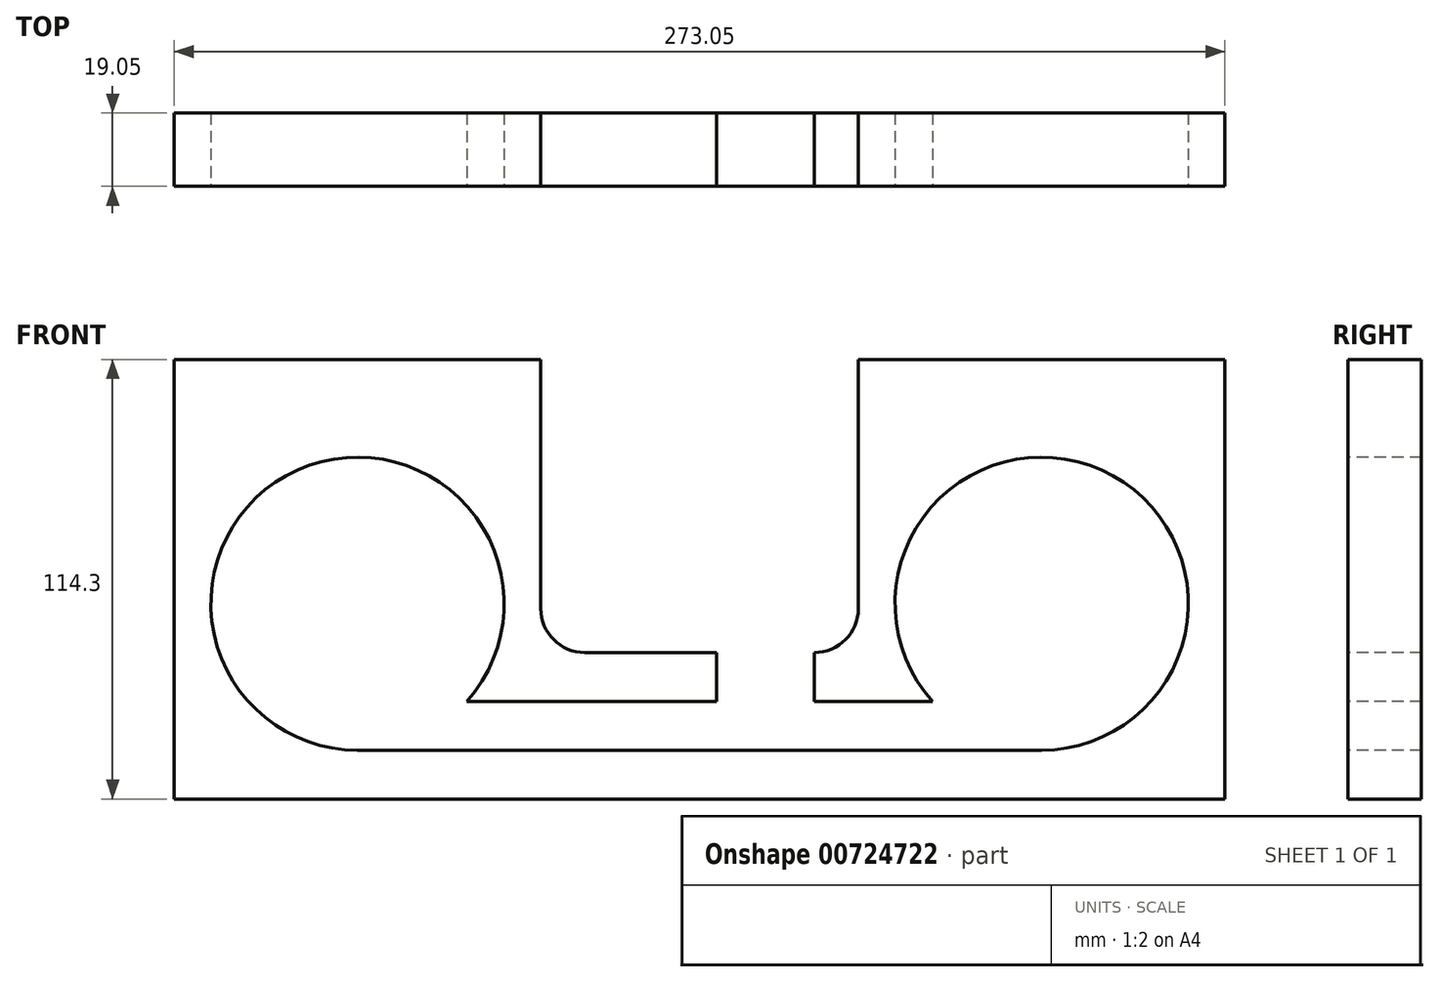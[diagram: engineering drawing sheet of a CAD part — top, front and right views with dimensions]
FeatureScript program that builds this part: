
annotation { "Feature Type Name" : "Feature", "Feature Type Description" : "" }
export const myFeature = defineFeature(function(context is Context, id is Id, definition is map)
    precondition{}
    {
        {
            var Q0;
            Q0=qCreatedBy(makeId("Front.planeOp"),FACE);
            var sketch = newSketch(context, id + "F0", { "sketchPlane" : qUnion([Q0])});
            skLineSegment(sketch, "E0.bottom", {"start": v(0, 0) * mm, "end": v(273.05, 0) * mm});
            skLineSegment(sketch, "E0.top", {"start": v(0, 114.3) * mm, "end": v(273.05, 114.3) * mm});
            skLineSegment(sketch, "E0.left", {"start": v(0, 0) * mm, "end": v(0, 114.3) * mm});
            skLineSegment(sketch, "E0.right", {"start": v(273.05, 0) * mm, "end": v(273.05, 114.3) * mm});
            skSolve(sketch);
        }
        {
            var Q0;
            Q0=qSketchRegion(id+"F0",true);
            extrude(context, id + "F1", {"entities" : qUnion([Q0]), "depth" : 19.05 * mm, "offsetDistance" : 25.4 * mm});
        }
        {
            var Q0;
            Q0=makeQuery(id+"F1.opExtrude","CAP_FACE",FACE,{"disambiguationData":[OSD([sQuery(id+"F0.wireOp",EDGE,"E0.bottom"),sQuery(id+"F0.wireOp",EDGE,"E0.top"),sQuery(id+"F0.wireOp",EDGE,"E0.left"),sQuery(id+"F0.wireOp",EDGE,"E0.right")])],"isStart":false});
            var sketch = newSketch(context, id + "F2", { "sketchPlane" : qUnion([Q0])});
            skCircle(sketch, "E1", {"center": v(47.63, 50.8) * mm, "radius": 38.1 * mm});
            skCircle(sketch, "E2", {"center": v(225.43, 50.8) * mm, "radius": 38.1 * mm});
            skSolve(sketch);
        }
        {
            var Q0;
            Q0=qSketchRegion(id+"F2",true);
            extrude(context, id + "F3", {"entities" : qUnion([Q0]), "operationType" : NewBodyOperationType.REMOVE, "oppositeDirection" : true, "depth" : 25.4 * mm, "offsetDistance" : 25.4 * mm});
        }
        {
            var Q0;
            Q0=makeQuery(id+"F1.opExtrude","CAP_FACE",FACE,{"disambiguationData":[OSD([sQuery(id+"F0.wireOp",EDGE,"E0.bottom"),sQuery(id+"F0.wireOp",EDGE,"E0.top"),sQuery(id+"F0.wireOp",EDGE,"E0.left"),sQuery(id+"F0.wireOp",EDGE,"E0.right")])],"isStart":false});
            var sketch = newSketch(context, id + "F4", { "sketchPlane" : qUnion([Q0])});
            skLineSegment(sketch, "E3", {"start": v(95.25, 114.3) * mm, "end": v(95.25, 49.53) * mm});
            skLineSegment(sketch, "E4", {"start": v(106.68, 38.1) * mm, "end": v(166.37, 38.1) * mm});
            skLineSegment(sketch, "E5", {"start": v(177.8, 49.53) * mm, "end": v(177.8, 114.3) * mm});
            skPoint(sketch, "E6.visualSharp", {"position": v(95.25, 38.1) * mm});
            skArc(sketch, "E6.filletArc", {"start": v(95.25, 49.53) * mm, "mid": v(98.6, 41.45) * mm, "end": v(106.68, 38.1) * mm});
            skPoint(sketch, "E7.visualSharp", {"position": v(177.8, 38.1) * mm});
            skArc(sketch, "E7.filletArc", {"start": v(166.37, 38.1) * mm, "mid": v(174.45, 41.45) * mm, "end": v(177.8, 49.53) * mm});
            skSolve(sketch);
        }
        {
            var Q0;
            Q0=qSketchRegion(id+"F4",true);
            var Q1;
            {var subQ1=sQuery(id+"F4.wireOp",EDGE,"E3");Q1=makeQuery(id+"F4.imprint","IMPRINT",FACE,{"disambiguationData":[TD([[makeQuery(id+"F4.imprint","IMPRINT",EDGE,{"derivedFrom":subQ1}),1.0]])]});}
            extrude(context, id + "F5", {"entities" : qUnion([Q0, Q1]), "operationType" : NewBodyOperationType.REMOVE, "oppositeDirection" : true, "depth" : 25.4 * mm, "offsetDistance" : 25.4 * mm});
        }
        {
            var Q0;
            Q0=makeQuery(id+"F1.opExtrude","CAP_FACE",FACE,{"disambiguationData":[OSD([sQuery(id+"F0.wireOp",EDGE,"E0.bottom"),sQuery(id+"F0.wireOp",EDGE,"E0.top"),sQuery(id+"F0.wireOp",EDGE,"E0.left"),sQuery(id+"F0.wireOp",EDGE,"E0.right")])],"isStart":false});
            var sketch = newSketch(context, id + "F6", { "sketchPlane" : qUnion([Q0])});
            skLineSegment(sketch, "E8", {"start": v(140.97, 38.1) * mm, "end": v(140.97, 25.4) * mm});
            skLineSegment(sketch, "E9", {"start": v(140.97, 25.4) * mm, "end": v(76.02, 25.4) * mm});
            skLineSegment(sketch, "E10", {"start": v(225.43, 12.7) * mm, "end": v(197.03, 25.4) * mm});
            skLineSegment(sketch, "E11", {"start": v(197.03, 25.4) * mm, "end": v(166.37, 25.4) * mm});
            skLineSegment(sketch, "E12", {"start": v(166.37, 25.4) * mm, "end": v(166.37, 38.1) * mm});
            skLineSegment(sketch, "E13", {"start": v(76.02, 25.4) * mm, "end": v(47.63, 12.7) * mm});
            skLineSegment(sketch, "E14", {"start": v(47.63, 12.7) * mm, "end": v(225.43, 12.7) * mm});
            skSolve(sketch);
        }
        {
            var Q0;
            Q0=qSketchRegion(id+"F6",true);
            var Q1;
            {var subQ3=sQuery(id+"F6.wireOp",EDGE,"E8");Q1=makeQuery(id+"F6.imprint","IMPRINT",FACE,{"disambiguationData":[TD([[makeQuery(id+"F6.imprint","IMPRINT",EDGE,{"derivedFrom":subQ3}),1.0]])]});}
            extrude(context, id + "F7", {"entities" : qUnion([Q0, Q1]), "operationType" : NewBodyOperationType.REMOVE, "oppositeDirection" : true, "depth" : 25.4 * mm, "offsetDistance" : 25.4 * mm});
        }
    });
